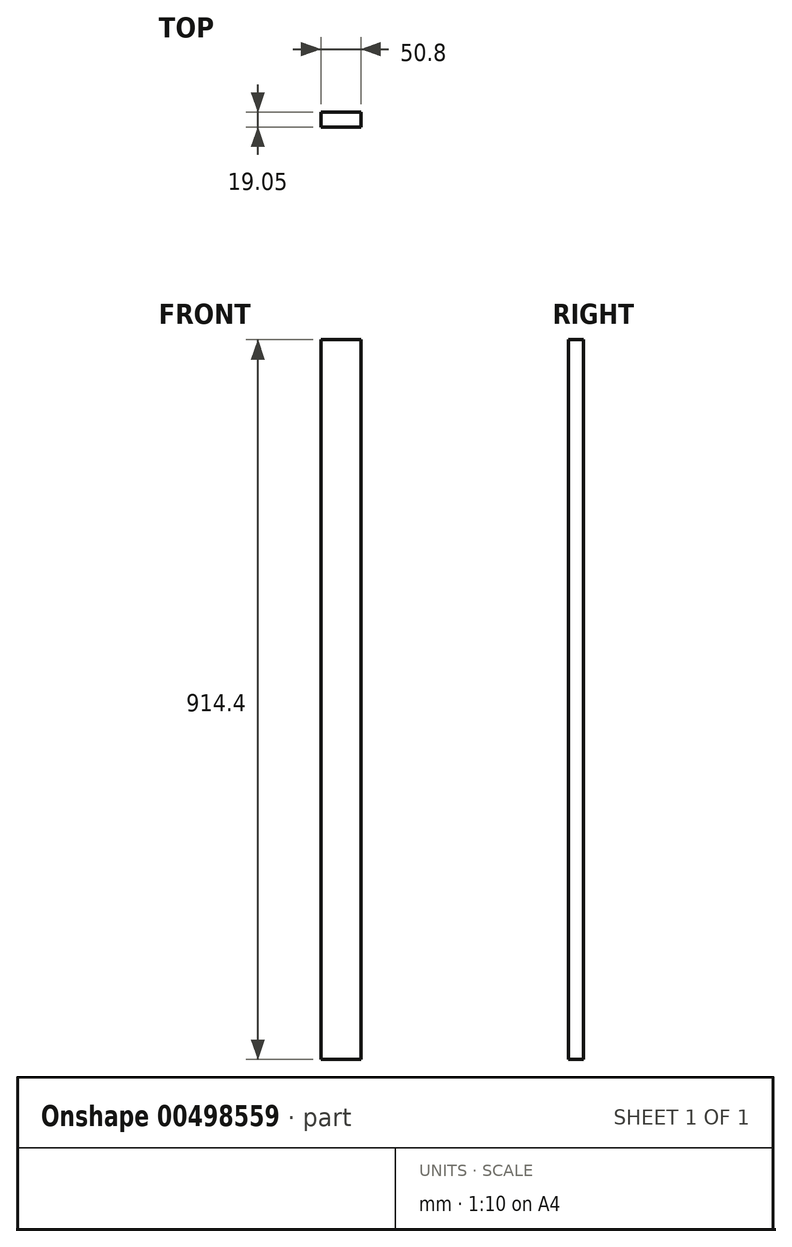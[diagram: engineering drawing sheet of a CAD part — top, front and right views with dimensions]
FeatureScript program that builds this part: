
annotation { "Feature Type Name" : "Feature", "Feature Type Description" : "" }
export const myFeature = defineFeature(function(context is Context, id is Id, definition is map)
    precondition{}
    {
        {
            var Q0;
            Q0=qCreatedBy(makeId("Front.planeOp"),FACE);
            var sketch = newSketch(context, id + "F0", { "sketchPlane" : qUnion([Q0])});
            skLineSegment(sketch, "E0.bottom", {"start": v(0, 0) * mm, "end": v(50.8, 0) * mm});
            skLineSegment(sketch, "E0.top", {"start": v(0, 914.4) * mm, "end": v(50.8, 914.4) * mm});
            skLineSegment(sketch, "E0.left", {"start": v(0, 0) * mm, "end": v(0, 914.4) * mm});
            skLineSegment(sketch, "E0.right", {"start": v(50.8, 0) * mm, "end": v(50.8, 914.4) * mm});
            skSolve(sketch);
        }
        {
            var Q0;
            Q0 = qSketchRegion(id + "F0", true);
            extrude(context, id + "F1", {"entities" : qUnion([Q0]), "depth" : 19.05 * mm, "offsetDistance" : 25.4 * mm});
        }
    });
